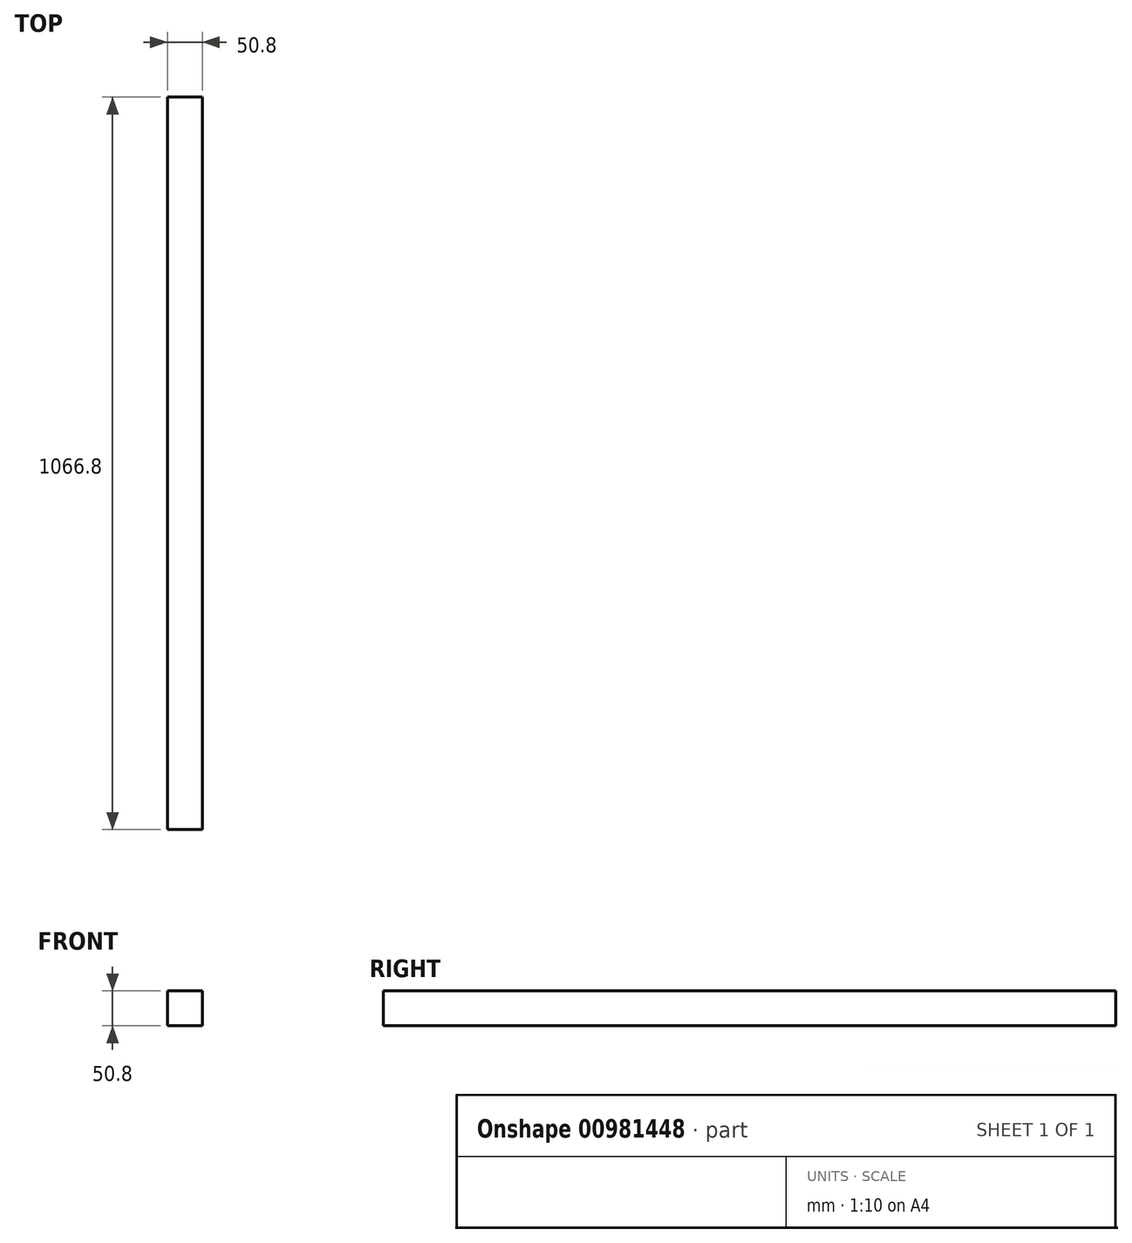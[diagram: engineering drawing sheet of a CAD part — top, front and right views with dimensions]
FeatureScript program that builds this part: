
annotation { "Feature Type Name" : "Feature", "Feature Type Description" : "" }
export const myFeature = defineFeature(function(context is Context, id is Id, definition is map)
    precondition{}
    {
        {
            var Q0;
            Q0=qCreatedBy(makeId("Front.planeOp"),FACE);
            var sketch = newSketch(context, id + "F0", { "sketchPlane" : qUnion([Q0])});
            skLineSegment(sketch, "E0.bottom", {"start": v(-25.4, 25.4) * mm, "end": v(25.4, 25.4) * mm});
            skLineSegment(sketch, "E0.top", {"start": v(-25.4, -25.4) * mm, "end": v(25.4, -25.4) * mm});
            skLineSegment(sketch, "E0.left", {"start": v(-25.4, 25.4) * mm, "end": v(-25.4, -25.4) * mm});
            skLineSegment(sketch, "E0.right", {"start": v(25.4, 25.4) * mm, "end": v(25.4, -25.4) * mm});
            skSolve(sketch);
        }
        {
            var Q0;
            Q0 = qSketchRegion(id + "F0", true);
            extrude(context, id + "F1", {"entities" : qUnion([Q0]), "oppositeDirection" : true, "depth" : 1066.8 * mm, "offsetDistance" : 25.4 * mm});
        }
    });
